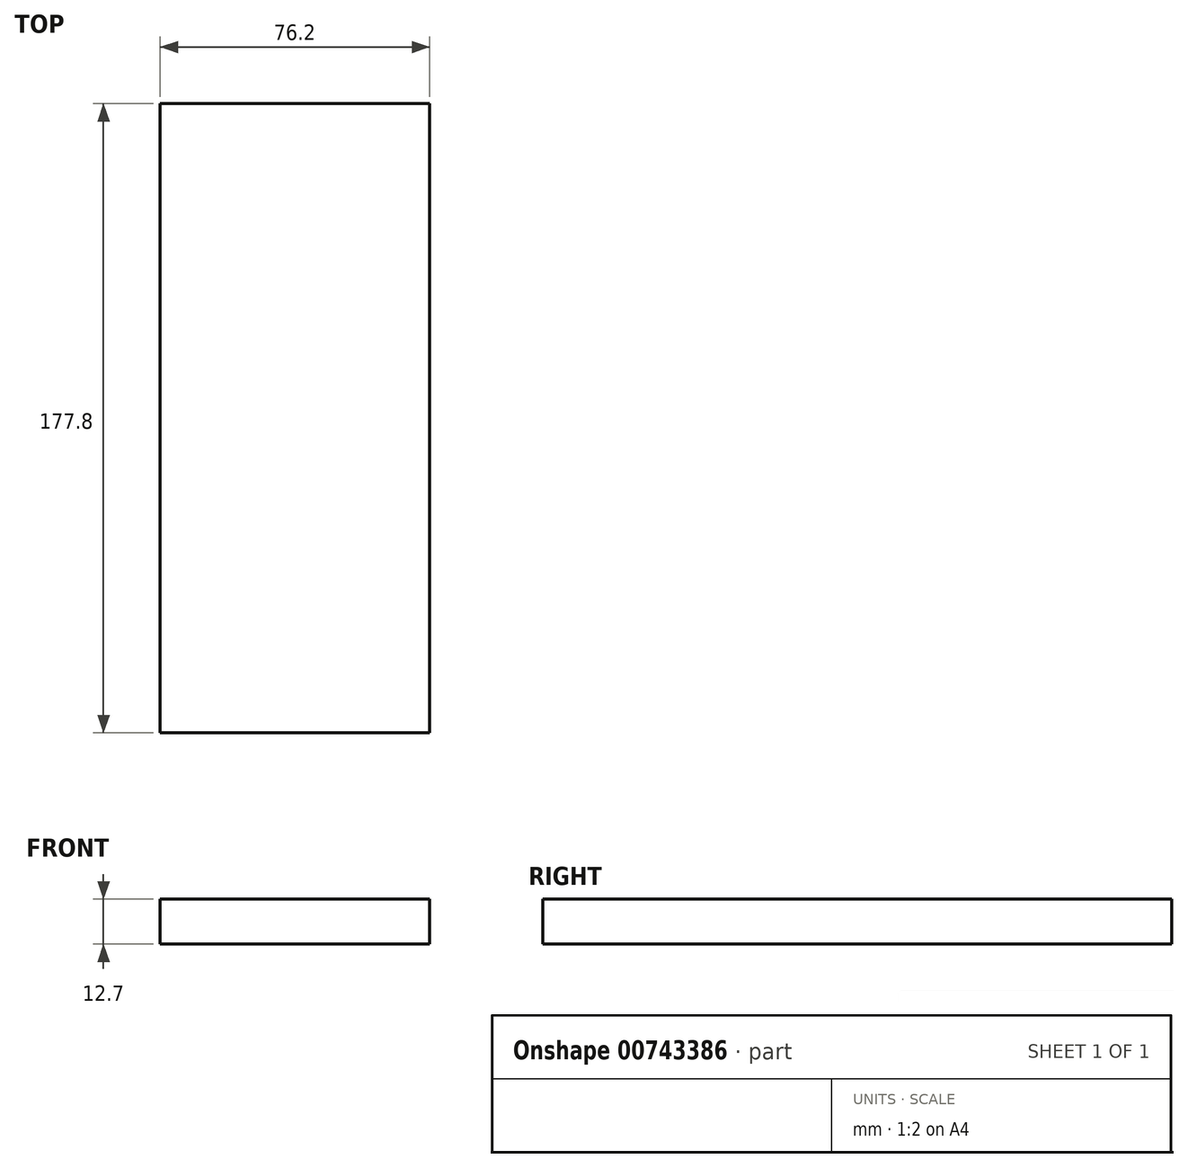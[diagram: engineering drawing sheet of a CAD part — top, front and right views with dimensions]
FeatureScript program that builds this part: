
annotation { "Feature Type Name" : "Feature", "Feature Type Description" : "" }
export const myFeature = defineFeature(function(context is Context, id is Id, definition is map)
    precondition{}
    {
        {
            var Q0;
            Q0=qCreatedBy(makeId("Top.planeOp"),FACE);
            var sketch = newSketch(context, id + "F0", { "sketchPlane" : qUnion([Q0])});
            skLineSegment(sketch, "E0.bottom", {"start": v(-76.2, 177.8) * mm, "end": v(0, 177.8) * mm});
            skLineSegment(sketch, "E0.top", {"start": v(-76.2, 0) * mm, "end": v(0, 0) * mm});
            skLineSegment(sketch, "E0.left", {"start": v(-76.2, 177.8) * mm, "end": v(-76.2, 0) * mm});
            skLineSegment(sketch, "E0.right", {"start": v(0, 177.8) * mm, "end": v(0, 0) * mm});
            skSolve(sketch);
        }
        {
            var Q0;
            Q0=makeQuery(id+"F0.imprint","IMPRINT",FACE,{"disambiguationData":[TD([[makeQuery(id+"F0.imprint","IMPRINT",EDGE,{"derivedFrom":sQuery(id+"F0.wireOp",EDGE,"E0.bottom")}),-1.0]])]});
            extrude(context, id + "F1", {"entities" : qUnion([Q0]), "depth" : 12.7 * mm, "offsetDistance" : 25.4 * mm});
        }
    });
